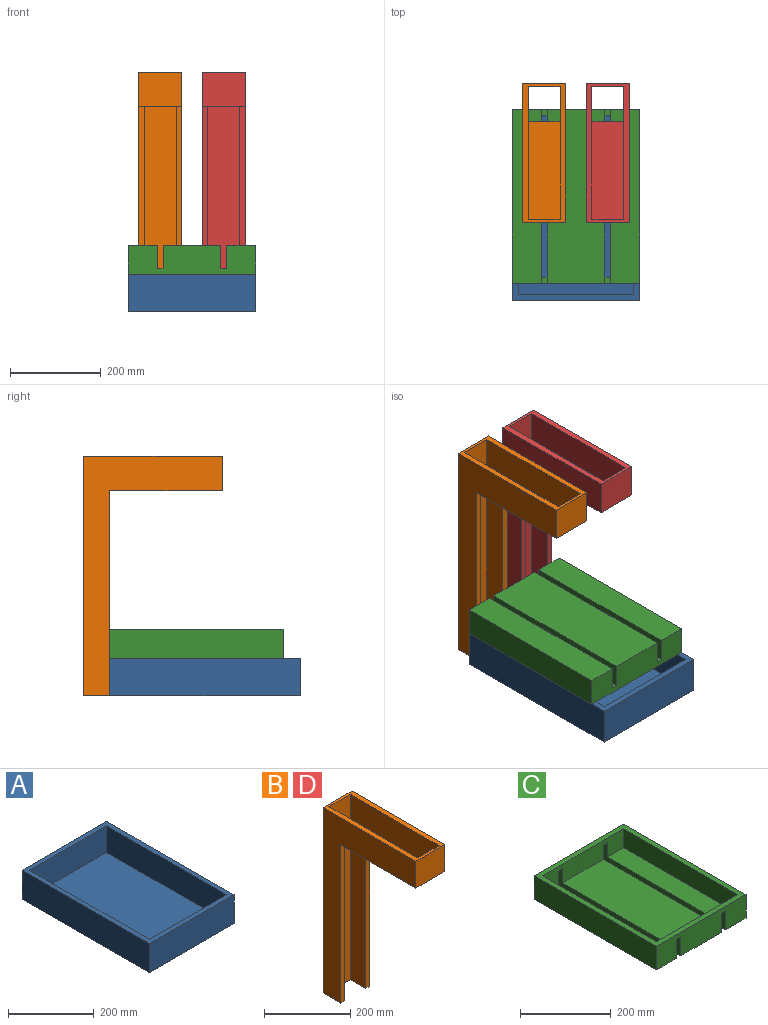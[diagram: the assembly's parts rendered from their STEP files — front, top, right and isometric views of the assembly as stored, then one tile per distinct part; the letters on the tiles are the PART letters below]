
ASSEMBLY  parts=4 mates=5
PART A: 11 faces, bbox 279.4x419.1x82.6 mm
  f0: plane 254x76.2mm, normal (0,-1,0), area 19354.8mm2, adj f1,f7,f8,f9
  f1: plane 393.7x76.2mm, normal (-1,0,0), area 29999.9mm2, adj f0,f2,f8,f9
  f2: plane 254x76.2mm, normal (0,1,0), area 19354.8mm2, adj f1,f7,f8,f9
  f3: plane 419.1x82.55mm, normal (1,0,0), area 34596.7mm2, adj f4,f6,f8,f10
  f4: plane 279.4x82.55mm, normal (0,1,0), area 23064.5mm2, adj f3,f5,f8,f10
  f5: plane 419.1x82.55mm, normal (-1,0,0), area 34596.7mm2, adj f4,f6,f8,f10
  f6: plane 279.4x82.55mm, normal (0,-1,0), area 23064.5mm2, adj f3,f5,f8,f10
  f7: plane 393.7x76.2mm, normal (1,0,0), area 29999.9mm2, adj f0,f2,f8,f9
  f8: plane 419.1x279.4mm, normal (0,0,1), area 17096.7mm2, adj f0,f1,f2,f3,f4,f5,f6,f7
  f9: plane 393.7x254mm, normal (0,0,1), area 99999.8mm2, adj f0,f1,f2,f7
  f10: plane 419.1x279.4mm, normal (0,0,-1), area 117096.5mm2, adj f3,f4,f5,f6
PART B: 15 faces, bbox 95.3x304.8x527.1 mm
  f0: plane 247.65x95.25mm, normal (0,0,-1), area 21814.5mm2, adj f3,f5,f7,f8,f9,f11,f12,f13
  f1: plane 215.9x69.85mm, normal (0,0,1), area 15080.6mm2, adj f3,f4,f9,f11
  f2: plane 527.05x69.85mm, normal (0,-1,0), area 36814.4mm2, adj f3,f9,f10,f14
  f3: plane 527.05x292.1mm, normal (-1,0,0), area 43790.2mm2, adj f0,f1,f2,f4,f10,f11,f12,f14
  f4: plane 69.85x69.85mm, normal (0,1,0), area 4879mm2, adj f1,f3,f9,f10
  f5: plane 527.05x304.8mm, normal (1,0,0), area 48991.8mm2, adj f0,f6,f8,f10,f12,f14
  f6: plane 527.05x95.25mm, normal (0,1,0), area 50201.5mm2, adj f5,f7,f10,f14
  f7: plane 527.05x304.8mm, normal (-1,0,0), area 48991.8mm2, adj f0,f6,f8,f10,f13,f14
  f8: plane 95.25x76.2mm, normal (0,-1,0), area 7258mm2, adj f0,f5,f7,f10
  f9: plane 527.05x292.1mm, normal (1,0,0), area 43790.2mm2, adj f0,f1,f2,f4,f10,f11,f13,f14
  f10: plane 304.8x95.25mm, normal (0,0,1), area 8629mm2, adj f2,f3,f4,f5,f6,f7,f8,f9
  f11: plane 69.85x6.35mm, normal (0,1,0), area 443.5mm2, adj f0,f1,f3,f9
  f12: plane 450.85x12.7mm, normal (0,-1,0), area 5725.8mm2, adj f0,f3,f5,f14
  f13: plane 450.85x12.7mm, normal (0,-1,0), area 5725.8mm2, adj f0,f7,f9,f14
  f14: plane 95.25x57.15mm, normal (0,0,-1), area 1895.2mm2, adj f2,f3,f5,f6,f7,f9,f12,f13
PART C: 23 faces, bbox 279.4x381x63.5 mm
  f0: plane 381x127mm, normal (0,0,-1), area 48387mm2, adj f4,f9,f16,f21
  f1: plane 381x63.5mm, normal (0,0,-1), area 24193.5mm2, adj f4,f9,f10,f20
  f2: plane 254x50.8mm, normal (0,-1,0), area 11935.5mm2, adj f5,f6,f7,f11,f12,f13,f16,f17
  f3: plane 254x50.8mm, normal (0,1,0), area 11935.5mm2, adj f5,f6,f7,f11,f12,f13,f15,f16
  f4: plane 279.4x63.5mm, normal (0,-1,0), area 16451.6mm2, adj f0,f1,f8,f10,f12,f14,f15,f16
  f5: plane 355.6x50.8mm, normal (0,0,1), area 18064.5mm2, adj f2,f3,f11,f20
  f6: plane 355.6x50.8mm, normal (0,0,1), area 18064.5mm2, adj f2,f3,f7,f17
  f7: plane 355.6x50.8mm, normal (-1,0,0), area 18064.5mm2, adj f2,f3,f6,f12
  f8: plane 381x63.5mm, normal (1,0,0), area 24193.5mm2, adj f4,f9,f12,f14
  f9: plane 279.4x63.5mm, normal (0,1,0), area 16451.6mm2, adj f0,f1,f8,f10,f12,f14,f16,f17
  f10: plane 381x63.5mm, normal (-1,0,0), area 24193.5mm2, adj f1,f4,f9,f12
  f11: plane 355.6x50.8mm, normal (1,0,0), area 18064.5mm2, adj f2,f3,f5,f12
  f12: plane 381x279.4mm, normal (0,0,1), area 16129mm2, adj f2,f3,f4,f7,f8,f9,f10,f11
  f13: plane 355.6x127mm, normal (0,0,1), area 45161.2mm2, adj f2,f3,f16,f21
  f14: plane 381x63.5mm, normal (0,0,-1), area 24193.5mm2, adj f4,f8,f9,f17
  f15: plane 12.7x12.7mm, normal (0,0,-1), area 161.3mm2, adj f3,f4,f16,f17
  f16: plane 381x50.8mm, normal (1,0,0), area 5806.4mm2, adj f0,f2,f3,f4,f9,f13,f15,f18
  f17: plane 381x50.8mm, normal (-1,0,0), area 5806.4mm2, adj f2,f3,f4,f6,f9,f14,f15,f18
  f18: plane 12.7x12.7mm, normal (0,0,-1), area 161.3mm2, adj f2,f9,f16,f17
  f19: plane 12.7x12.7mm, normal (0,0,-1), area 161.3mm2, adj f3,f4,f20,f21
  f20: plane 381x50.8mm, normal (1,0,0), area 5806.4mm2, adj f1,f2,f3,f4,f5,f9,f19,f22
  f21: plane 381x50.8mm, normal (-1,0,0), area 5806.4mm2, adj f0,f2,f3,f4,f9,f13,f19,f22
  f22: plane 12.7x12.7mm, normal (0,0,-1), area 161.3mm2, adj f2,f9,f20,f21
PART D: same geometry as B
PLACE A t=(42.43,33.18,-13.71)mm
PLACE B t=(-21.8,147.48,437.14)mm
PLACE C rot(axis=(0,1,0),180deg) t=(48.05,52.23,113.29)mm
PLACE D t=(117.9,147.48,437.14)mm
MATE planar C.f12 <-> A.f8  axis (0,0,-1) through (48.05,52.23,62.49)mm
MATE planar C.f9 <-> A.f4  axis (0,1,0) through (48.05,242.73,62.49)mm
MATE planar C.f10 <-> A.f3  axis (1,0,0) through (187.75,52.23,62.49)mm
MATE fastened D.f12 <-> A.f4  axis (0,-1,0) through (165.52,242.73,-20.06)mm
MATE fastened B.f13 <-> A.f4  axis (0,-1,0) through (-69.43,242.73,-20.06)mm
